# Revit family: RUE2_63_UN_Light-pole_ETK
name_source: partatom
category: Lighting Fixtures
revit_build: Autodesk Revit 2017 (Build: 20190508_0315(x64)
units: mm (PartAtom-declared; Revit-internal decimal feet)

## family parameters
Always vertical = Yes
Cut with Voids When Loaded = No
Light Source = No
OmniClass Number = 23.80.70.11.14.11
OmniClass Title = Downlights
Part Type = Normal
Room Calculation Point = Yes
Round Connector Dimension = Use Diameter
Shared = No
Work Plane-Based = No

## types (14) — shared parameters
Assembly Code = 63.0
Bundle = 180° - 360°
Description = Light Pole
IfcExportAs = IfcLightFixtureType
IfcExportType = USERDEFINED
Lamp = LED
Luminaire_Body_Material = RAL9006
Manufacturer = ETK licht B.V.
Model = RUE.2
Pole_Material = RAL7024
URL = https://www.etk.nl
Voltage = 230 V

## per-type parameters (varying)
| type | Apparent Load | Light Source | Wattage Comments |
| RUE.2110.25 - 25W / 2800lm / 3000K | 25 VA | RUE2 Lamp + Gimble : RUE.2110.25 - 25W / 2800lm / 3000K | 25W |
| RUE.2120.25 - 25W / 2950lm / 4000K | 25 VA | RUE2 Lamp + Gimble : RUE.2120.25 - 25W / 2950lm / 4000K | 25W |
| RUE.2210.25 - 35W / 3750lm / 3000K | 35 VA | RUE2 Lamp + Gimble : RUE.2210.25 - 35W / 3750lm / 3000K | 35W |
| RUE.2220.25 - 35W / 3950lm / 4000K | 35 VA | RUE2 Lamp + Gimble : RUE.2220.25 - 35W / 3950lm / 4000K | 35W |
| RUE.2310.25 - 44W / 4600lm / 3000K | 44 VA | RUE2 Lamp + Gimble : RUE.2310.25 - 44W / 4600lm / 3000K | 44W |
| RUE.2320.25 - 44W / 4900lm / 4000K | 44 VA | RUE2 Lamp + Gimble : RUE.2320.25 - 44W / 4900lm / 4000K | 44W |
| RUE.2410.25 - 59W / 7000lm / 3000K | 59 VA | RUE2 Lamp + Gimble : RUE.2410.25 - 59W / 7000lm / 3000K | 59W |
| RUE.2420.25 - 59W / 7350lm / 4000K | 59 VA | RUE2 Lamp + Gimble : RUE.2420.25 - 59W / 7350lm / 4000K | 59W |
| RUE.2510.25 - 71W / 8400lm / 3000K | 71 VA | RUE2 Lamp + Gimble : RUE.2510.25 - 71W / 8400lm / 3000K | 71W |
| RUE.2520.25 - 71W / 8750lm / 4000K | 71 VA | RUE2 Lamp + Gimble : RUE.2520.25 - 71W / 8750lm / 4000K | 71W |
| RUE.2610.25 - 87W / 10400lm / 3000K | 87 VA | RUE2 Lamp + Gimble : RUE.2610.25 - 87W / 10400lm / 3000K | 87W |
| RUE.2620.25 - 87W / 10850lm / 4000K | 87 VA | RUE2 Lamp + Gimble : RUE.2620.25 - 87W / 10850lm / 4000K | 87W |
| RUE.2710.25 - 122W / 13650lm / 3000K | 122 VA | RUE2 Lamp + Gimble : RUE.2710.25 - 122W / 13650lm / 3000K | 122W |
| RUE.2720.25 - 122W / 14250lm / 4000K | 25 VA | RUE2 Lamp + Gimble : RUE.2720.25 - 122W / 14250lm / 4000K | 25W |

## geometry (parser evidence)
native form markers: Sweep x10
no freeform markers — native parametric forms only
